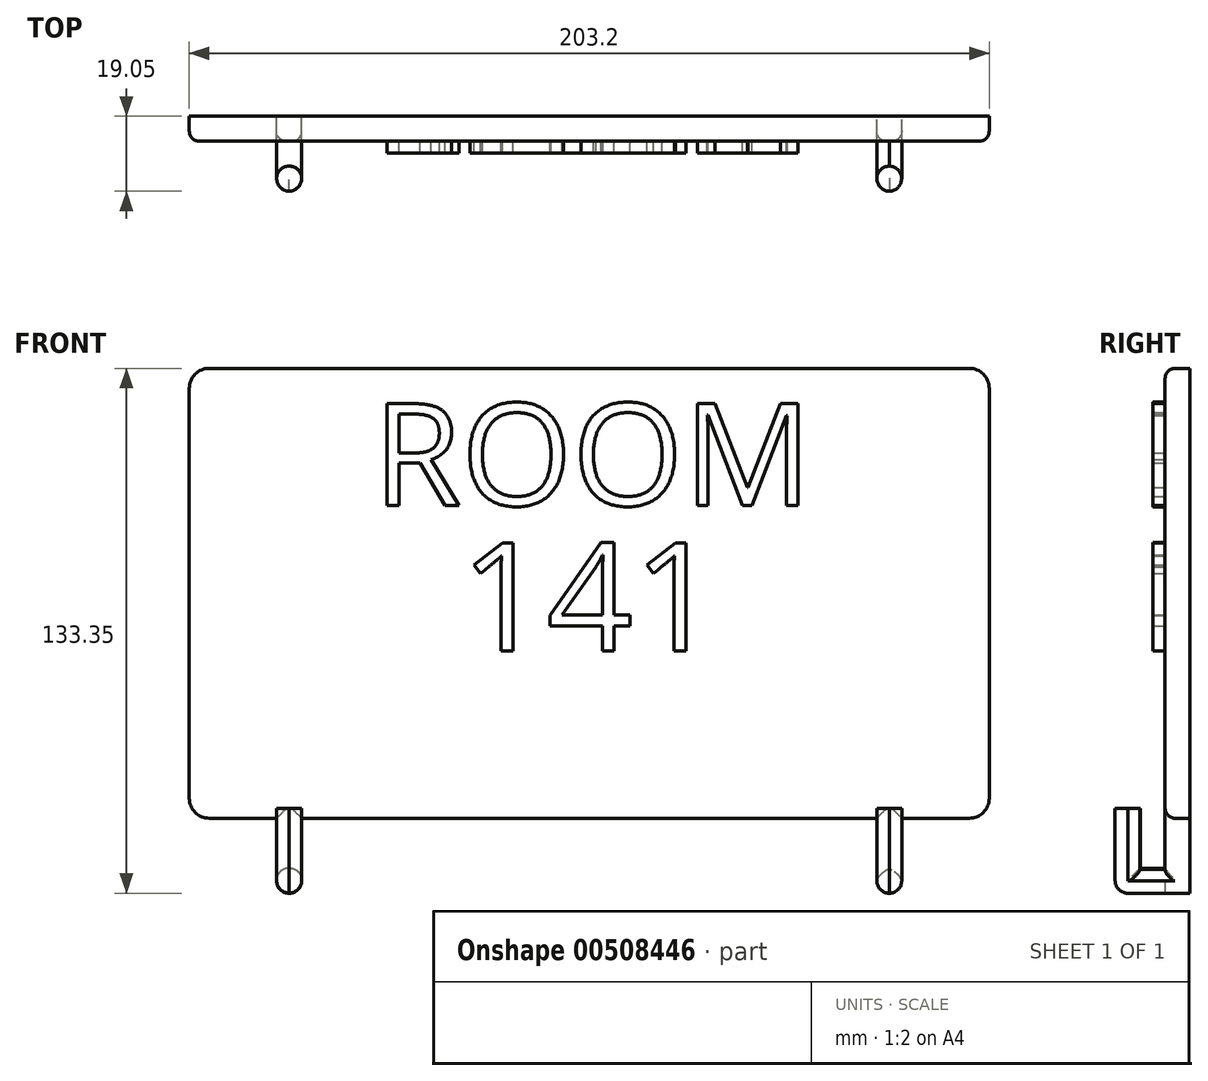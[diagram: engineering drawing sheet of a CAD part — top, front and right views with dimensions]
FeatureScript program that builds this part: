
annotation { "Feature Type Name" : "Feature", "Feature Type Description" : "" }
export const myFeature = defineFeature(function(context is Context, id is Id, definition is map)
    precondition{}
    {
        {
            var Q0;
            Q0=qCreatedBy(makeId("Front.planeOp"),FACE);
            var sketch = newSketch(context, id + "F0", { "sketchPlane" : qUnion([Q0])});
            skLineSegment(sketch, "E0.bottom", {"start": v(101.6, 57.15) * mm, "end": v(-101.6, 57.15) * mm});
            skLineSegment(sketch, "E0.top", {"start": v(101.6, -57.15) * mm, "end": v(-101.6, -57.15) * mm});
            skLineSegment(sketch, "E0.left", {"start": v(101.6, 57.15) * mm, "end": v(101.6, -57.15) * mm});
            skLineSegment(sketch, "E0.right", {"start": v(-101.6, 57.15) * mm, "end": v(-101.6, -57.15) * mm});
            skPoint(sketch, "E0.middle", {"position": v(0, 0) * mm});
            skSolve(sketch);
        }
        {
            var Q0;
            Q0=makeQuery(id+"F0.imprint","IMPRINT",FACE,{"disambiguationData":[TD([[makeQuery(id+"F0.imprint","IMPRINT",EDGE,{"derivedFrom":sQuery(id+"F0.wireOp",EDGE,"E0.bottom")}),1.0]])]});
            extrude(context, id + "F1", {"entities" : qUnion([Q0]), "depth" : 6.35 * mm});
        }
        {
            var Q0;
            Q0=makeQuery(id+"F1.opExtrude","SWEPT_FACE",FACE,{"disambiguationData":[OSD([sQuery(id+"F0.wireOp",EDGE,"E0.top")])]});
            var sketch = newSketch(context, id + "F2", { "sketchPlane" : qUnion([Q0])});
            skLineSegment(sketch, "E1.bottom", {"start": v(-73.07, 6.35) * mm, "end": v(-79.42, 6.35) * mm});
            skLineSegment(sketch, "E1.top", {"start": v(-73.07, 0) * mm, "end": v(-79.42, 0) * mm});
            skLineSegment(sketch, "E1.left", {"start": v(-73.07, 6.35) * mm, "end": v(-73.07, 0) * mm});
            skLineSegment(sketch, "E1.right", {"start": v(-79.42, 6.35) * mm, "end": v(-79.42, 0) * mm});
            skPoint(sketch, "E1.middle", {"position": v(-76.24, 3.17) * mm});
            skLineSegment(sketch, "E2.bottom", {"start": v(79.39, 6.35) * mm, "end": v(73.04, 6.35) * mm});
            skLineSegment(sketch, "E2.top", {"start": v(79.39, 0) * mm, "end": v(73.04, 0) * mm});
            skLineSegment(sketch, "E2.left", {"start": v(79.39, 6.35) * mm, "end": v(79.39, 0) * mm});
            skLineSegment(sketch, "E2.right", {"start": v(73.04, 6.35) * mm, "end": v(73.04, 0) * mm});
            skPoint(sketch, "E2.middle", {"position": v(76.21, 3.18) * mm});
            skSolve(sketch);
        }
        {
            var Q0;
            Q0 = qSketchRegion(id + "F2", true);
            extrude(context, id + "F3", {"entities" : qUnion([Q0]), "operationType" : NewBodyOperationType.ADD, "depth" : 19.05 * mm});
        }
        {
            var Q0;
            Q0=makeQuery(id+"F3.boolean.opBoolean","MERGE",FACE,{"derivedFrom":[makeQuery(id+"F1.opExtrude","CAP_FACE",FACE,{"disambiguationData":[OSD([sQuery(id+"F0.wireOp",EDGE,"E0.bottom"),sQuery(id+"F0.wireOp",EDGE,"E0.top"),sQuery(id+"F0.wireOp",EDGE,"E0.left"),sQuery(id+"F0.wireOp",EDGE,"E0.right")])],"isStart":false}),makeQuery(id+"F3.opExtrude","SWEPT_FACE",FACE,{"disambiguationData":[OSD([sQuery(id+"F2.wireOp",EDGE,"E1.bottom")])]}),makeQuery(id+"F3.opExtrude","SWEPT_FACE",FACE,{"disambiguationData":[OSD([sQuery(id+"F2.wireOp",EDGE,"E2.bottom")])]})]});
            var sketch = newSketch(context, id + "F4", { "sketchPlane" : qUnion([Q0])});
            skLineSegment(sketch, "E3.bottom", {"start": v(-79.42, -76.18) * mm, "end": v(-73.07, -76.18) * mm});
            skLineSegment(sketch, "E3.top", {"start": v(-79.42, -69.83) * mm, "end": v(-73.07, -69.83) * mm});
            skLineSegment(sketch, "E3.left", {"start": v(-79.42, -76.18) * mm, "end": v(-79.42, -69.83) * mm});
            skLineSegment(sketch, "E3.right", {"start": v(-73.07, -76.18) * mm, "end": v(-73.07, -69.83) * mm});
            skPoint(sketch, "E3.middle", {"position": v(-76.24, -73) * mm});
            skPoint(sketch, "E3.middle.positionSnap0", {"position": v(-76.24, -76.2) * mm});
            skPoint(sketch, "E3.centerSnap0", {"position": v(-76.24, -76.2) * mm});
            skPoint(sketch, "E4.cornerSnap0", {"position": v(79.39, -66.68) * mm});
            skPoint(sketch, "E5", {"position": v(76.21, -76.2) * mm});
            skLineSegment(sketch, "E6.bottom", {"start": v(73.04, -76.2) * mm, "end": v(79.39, -76.2) * mm});
            skLineSegment(sketch, "E6.top", {"start": v(73.04, -69.85) * mm, "end": v(79.39, -69.85) * mm});
            skLineSegment(sketch, "E6.left", {"start": v(73.04, -76.2) * mm, "end": v(73.04, -69.85) * mm});
            skLineSegment(sketch, "E6.right", {"start": v(79.39, -76.2) * mm, "end": v(79.39, -69.85) * mm});
            skSolve(sketch);
        }
        {
            var Q0;
            Q0 = qSketchRegion(id + "F4", true);
            extrude(context, id + "F5", {"entities" : qUnion([Q0]), "operationType" : NewBodyOperationType.ADD, "depth" : 12.7 * mm});
        }
        {
            var Q0;
            Q0=makeQuery(id+"F5.opExtrude","SWEPT_FACE",FACE,{"disambiguationData":[OSD([sQuery(id+"F4.wireOp",EDGE,"E6.top")])]});
            var sketch = newSketch(context, id + "F6", { "sketchPlane" : qUnion([Q0])});
            skLineSegment(sketch, "E7.bottom", {"start": v(73.04, -19.05) * mm, "end": v(79.39, -19.05) * mm});
            skLineSegment(sketch, "E7.top", {"start": v(73.04, -12.7) * mm, "end": v(79.39, -12.7) * mm});
            skLineSegment(sketch, "E7.left", {"start": v(73.04, -19.05) * mm, "end": v(73.04, -12.7) * mm});
            skLineSegment(sketch, "E7.right", {"start": v(79.39, -19.05) * mm, "end": v(79.39, -12.7) * mm});
            skLineSegment(sketch, "E8.bottom", {"start": v(-79.42, -19.04) * mm, "end": v(-73.07, -19.04) * mm});
            skLineSegment(sketch, "E8.top", {"start": v(-79.42, -12.7) * mm, "end": v(-73.07, -12.7) * mm});
            skLineSegment(sketch, "E8.left", {"start": v(-79.42, -19.04) * mm, "end": v(-79.42, -12.7) * mm});
            skLineSegment(sketch, "E8.right", {"start": v(-73.07, -19.04) * mm, "end": v(-73.07, -12.7) * mm});
            skSolve(sketch);
        }
        {
            var Q0;
            Q0 = qSketchRegion(id + "F6", true);
            extrude(context, id + "F7", {"entities" : qUnion([Q0]), "operationType" : NewBodyOperationType.ADD, "depth" : 15.24 * mm, "offsetDistance" : 25.4 * mm});
        }
        {
            var Q0;
            Q0=makeQuery(id+"F7.opExtrude","SWEPT_EDGE",EDGE,{"disambiguationData":[OSD([sQuery(id+"F6.wireOp",EDGE,"E8.bottom"),sQuery(id+"F6.wireOp",EDGE,"E8.left")])]});
            var Q1;
            Q1=makeQuery(id+"F7.opExtrude","SWEPT_EDGE",EDGE,{"disambiguationData":[OSD([sQuery(id+"F6.wireOp",EDGE,"E8.bottom"),sQuery(id+"F6.wireOp",EDGE,"E8.right")])]});
            fillet(context, id + "F8", {"entities" : qUnion([Q0, Q1]), "radius" : 3.3 * mm, "tangentPropagation" : true, "allowEdgeOverflow" : false});
        }
        {
            var Q0;
            Q0=makeQuery(id+"F5.opExtrude","SWEPT_EDGE",EDGE,{"disambiguationData":[OSD([sQuery(id+"F0.wireOp",EDGE,"E0.top"),sQuery(id+"F2.wireOp",EDGE,"E1.bottom"),sQuery(id+"F2.wireOp",EDGE,"E1.left"),sQuery(id+"F4.wireOp",EDGE,"E3.bottom"),sQuery(id+"F4.wireOp",EDGE,"E3.right")])]});
            var Q1;
            Q1=makeQuery(id+"F5.opExtrude","SWEPT_EDGE",EDGE,{"disambiguationData":[OSD([sQuery(id+"F0.wireOp",EDGE,"E0.top"),sQuery(id+"F2.wireOp",EDGE,"E1.bottom"),sQuery(id+"F2.wireOp",EDGE,"E1.right"),sQuery(id+"F4.wireOp",EDGE,"E3.bottom"),sQuery(id+"F4.wireOp",EDGE,"E3.left")])]});
            fillet(context, id + "F9", {"entities" : qUnion([Q0, Q1]), "radius" : 3.17 * mm, "tangentPropagation" : true, "allowEdgeOverflow" : false});
        }
        {
            var Q0;
            Q0=makeQuery(id+"F3.opExtrude","CAP_EDGE",EDGE,{"disambiguationData":[OSD([sQuery(id+"F2.wireOp",EDGE,"E1.left")])],"isStart":false});
            var Q1;
            Q1=makeQuery(id+"F3.opExtrude","CAP_EDGE",EDGE,{"disambiguationData":[OSD([sQuery(id+"F2.wireOp",EDGE,"E1.right")])],"isStart":false});
            fillet(context, id + "F10", {"entities" : qUnion([Q0, Q1]), "radius" : 3.17 * mm, "tangentPropagation" : true, "allowEdgeOverflow" : false});
        }
        {
            var Q0;
            Q0=makeQuery(id+"F7.opExtrude","SWEPT_EDGE",EDGE,{"disambiguationData":[OSD([sQuery(id+"F6.wireOp",EDGE,"E8.top"),sQuery(id+"F6.wireOp",EDGE,"E8.left")])]});
            var Q1;
            Q1=makeQuery(id+"F7.opExtrude","SWEPT_EDGE",EDGE,{"disambiguationData":[OSD([sQuery(id+"F6.wireOp",EDGE,"E8.top"),sQuery(id+"F6.wireOp",EDGE,"E8.right")])]});
            var Q2;
            {var subQ0=sQuery(id+"F2.wireOp",EDGE,"E1.right");var subQ1=sQuery(id+"F4.wireOp",EDGE,"E3.top");var subQ2=sQuery(id+"F4.wireOp",EDGE,"E3.left");Q2=makeQuery(id+"F7.boolean.opBoolean","SPLIT",EDGE,{"disambiguationData":[topologyDisambiguationEdgeConnected([makeQuery(id+"F5.opExtrude","SWEPT_FACE",FACE,{"disambiguationData":[OSD([subQ1])]})])],"derivedFrom":makeQuery(id+"F5.opExtrude","SWEPT_EDGE",EDGE,{"disambiguationData":[OSD([sQuery(id+"F0.wireOp",EDGE,"E0.top"),sQuery(id+"F2.wireOp",EDGE,"E1.bottom"),subQ0,subQ1,subQ2])]})});}
            var Q3;
            {var subQ0=sQuery(id+"F2.wireOp",EDGE,"E1.left");var subQ1=sQuery(id+"F4.wireOp",EDGE,"E3.right");var subQ2=sQuery(id+"F4.wireOp",EDGE,"E3.top");Q3=makeQuery(id+"F7.boolean.opBoolean","SPLIT",EDGE,{"disambiguationData":[topologyDisambiguationEdgeConnected([makeQuery(id+"F5.opExtrude","SWEPT_FACE",FACE,{"disambiguationData":[OSD([subQ2])]})])],"derivedFrom":makeQuery(id+"F5.opExtrude","SWEPT_EDGE",EDGE,{"disambiguationData":[OSD([sQuery(id+"F0.wireOp",EDGE,"E0.top"),sQuery(id+"F2.wireOp",EDGE,"E1.bottom"),subQ0,subQ2,subQ1])]})});}
            fillet(context, id + "F11", {"entities" : qUnion([Q0, Q1, Q2, Q3]), "radius" : 3.05 * mm, "tangentPropagation" : true, "allowEdgeOverflow" : false});
        }
        {
            var Q0;
            Q0=makeQuery(id+"F7.boolean.opBoolean","MERGE",EDGE,{"derivedFrom":[makeQuery(id+"F5.opExtrude","CAP_EDGE",EDGE,{"disambiguationData":[OSD([sQuery(id+"F4.wireOp",EDGE,"E6.left")])],"isStart":false}),makeQuery(id+"F7.opExtrude","SWEPT_EDGE",EDGE,{"disambiguationData":[OSD([sQuery(id+"F6.wireOp",EDGE,"E7.bottom"),sQuery(id+"F6.wireOp",EDGE,"E7.left")])]})]});
            var Q1;
            Q1=makeQuery(id+"F7.boolean.opBoolean","MERGE",EDGE,{"derivedFrom":[makeQuery(id+"F5.opExtrude","CAP_EDGE",EDGE,{"disambiguationData":[OSD([sQuery(id+"F4.wireOp",EDGE,"E6.right")])],"isStart":false}),makeQuery(id+"F7.opExtrude","SWEPT_EDGE",EDGE,{"disambiguationData":[OSD([sQuery(id+"F6.wireOp",EDGE,"E7.bottom"),sQuery(id+"F6.wireOp",EDGE,"E7.right")])]})]});
            fillet(context, id + "F12", {"entities" : qUnion([Q0, Q1]), "radius" : 3.3 * mm, "tangentPropagation" : true, "allowEdgeOverflow" : false});
        }
        {
            var Q0;
            Q0=makeQuery(id+"F7.opExtrude","SWEPT_EDGE",EDGE,{"disambiguationData":[OSD([sQuery(id+"F0.wireOp",EDGE,"E0.top"),sQuery(id+"F2.wireOp",EDGE,"E2.bottom"),sQuery(id+"F2.wireOp",EDGE,"E2.left"),sQuery(id+"F4.wireOp",EDGE,"E6.top"),sQuery(id+"F4.wireOp",EDGE,"E6.right"),sQuery(id+"F6.wireOp",EDGE,"E7.top"),sQuery(id+"F6.wireOp",EDGE,"E7.right")])]});
            var Q1;
            Q1=makeQuery(id+"F7.opExtrude","SWEPT_EDGE",EDGE,{"disambiguationData":[OSD([sQuery(id+"F0.wireOp",EDGE,"E0.top"),sQuery(id+"F2.wireOp",EDGE,"E2.bottom"),sQuery(id+"F2.wireOp",EDGE,"E2.right"),sQuery(id+"F4.wireOp",EDGE,"E6.top"),sQuery(id+"F4.wireOp",EDGE,"E6.left"),sQuery(id+"F6.wireOp",EDGE,"E7.top"),sQuery(id+"F6.wireOp",EDGE,"E7.left")])]});
            fillet(context, id + "F13", {"entities" : qUnion([Q0, Q1]), "radius" : 3.17 * mm, "tangentPropagation" : true, "allowEdgeOverflow" : false});
        }
        {
            var Q0;
            Q0=makeQuery(id+"F5.boolean.opBoolean","MERGE",EDGE,{"derivedFrom":[makeQuery(id+"F3.opExtrude","CAP_EDGE",EDGE,{"disambiguationData":[OSD([sQuery(id+"F2.wireOp",EDGE,"E2.right")])],"isStart":false}),makeQuery(id+"F5.opExtrude","SWEPT_EDGE",EDGE,{"disambiguationData":[OSD([sQuery(id+"F4.wireOp",EDGE,"E6.bottom"),sQuery(id+"F4.wireOp",EDGE,"E6.left")])]})]});
            var Q1;
            Q1=makeQuery(id+"F5.boolean.opBoolean","MERGE",EDGE,{"derivedFrom":[makeQuery(id+"F3.opExtrude","CAP_EDGE",EDGE,{"disambiguationData":[OSD([sQuery(id+"F2.wireOp",EDGE,"E2.left")])],"isStart":false}),makeQuery(id+"F5.opExtrude","SWEPT_EDGE",EDGE,{"disambiguationData":[OSD([sQuery(id+"F4.wireOp",EDGE,"E6.bottom"),sQuery(id+"F4.wireOp",EDGE,"E6.right")])]})]});
            fillet(context, id + "F14", {"entities" : qUnion([Q0, Q1]), "radius" : 3.17 * mm, "tangentPropagation" : true, "allowEdgeOverflow" : false});
        }
        {
            var Q0;
            Q0=makeQuery(id+"F5.opExtrude","SWEPT_EDGE",EDGE,{"disambiguationData":[OSD([sQuery(id+"F0.wireOp",EDGE,"E0.top"),sQuery(id+"F2.wireOp",EDGE,"E2.bottom"),sQuery(id+"F2.wireOp",EDGE,"E2.right"),sQuery(id+"F4.wireOp",EDGE,"E6.top"),sQuery(id+"F4.wireOp",EDGE,"E6.left")])]});
            var Q1;
            Q1=makeQuery(id+"F5.opExtrude","SWEPT_EDGE",EDGE,{"disambiguationData":[OSD([sQuery(id+"F0.wireOp",EDGE,"E0.top"),sQuery(id+"F2.wireOp",EDGE,"E2.bottom"),sQuery(id+"F2.wireOp",EDGE,"E2.left"),sQuery(id+"F4.wireOp",EDGE,"E6.top"),sQuery(id+"F4.wireOp",EDGE,"E6.right")])]});
            fillet(context, id + "F15", {"entities" : qUnion([Q0, Q1]), "radius" : 5.08 * mm, "tangentPropagation" : true, "allowEdgeOverflow" : false});
        }
        {
            var Q0;
            Q0=makeQuery(id+"F1.opExtrude","SWEPT_EDGE",EDGE,{"disambiguationData":[OSD([sQuery(id+"F0.wireOp",EDGE,"E0.top"),sQuery(id+"F0.wireOp",EDGE,"E0.left")])]});
            var Q1;
            Q1=makeQuery(id+"F1.opExtrude","SWEPT_EDGE",EDGE,{"disambiguationData":[OSD([sQuery(id+"F0.wireOp",EDGE,"E0.bottom"),sQuery(id+"F0.wireOp",EDGE,"E0.left")])]});
            var Q2;
            Q2=makeQuery(id+"F1.opExtrude","SWEPT_EDGE",EDGE,{"disambiguationData":[OSD([sQuery(id+"F0.wireOp",EDGE,"E0.bottom"),sQuery(id+"F0.wireOp",EDGE,"E0.right")])]});
            var Q3;
            Q3=makeQuery(id+"F1.opExtrude","SWEPT_EDGE",EDGE,{"disambiguationData":[OSD([sQuery(id+"F0.wireOp",EDGE,"E0.top"),sQuery(id+"F0.wireOp",EDGE,"E0.right")])]});
            fillet(context, id + "F16", {"entities" : qUnion([Q0, Q1, Q2, Q3]), "radius" : 5.08 * mm, "tangentPropagation" : true, "allowEdgeOverflow" : false});
        }
        {
            var Q0;
            Q0=makeQuery(id+"F1.opExtrude","CAP_EDGE",EDGE,{"disambiguationData":[OSD([sQuery(id+"F0.wireOp",EDGE,"E0.bottom")])],"isStart":false});
            var Q1;
            {var subQ0=sQuery(id+"F0.wireOp",EDGE,"E0.top");Q1=makeQuery(id+"F3.boolean.opBoolean","SPLIT",EDGE,{"disambiguationData":[TD([makeQuery(id+"F3.opExtrude","SWEPT_FACE",FACE,{"disambiguationData":[OSD([sQuery(id+"F2.wireOp",EDGE,"E1.left")])]})])],"derivedFrom":makeQuery(id+"F1.opExtrude","CAP_EDGE",EDGE,{"disambiguationData":[OSD([subQ0])],"isStart":false})});}
            var Q2;
            Q2=makeQuery(id+"F3.opExtrude","SWEPT_EDGE",EDGE,{"disambiguationData":[OSD([sQuery(id+"F0.wireOp",EDGE,"E0.top"),sQuery(id+"F2.wireOp",EDGE,"E2.bottom"),sQuery(id+"F2.wireOp",EDGE,"E2.right")])]});
            var Q3;
            Q3=makeQuery(id+"F3.opExtrude","SWEPT_EDGE",EDGE,{"disambiguationData":[OSD([sQuery(id+"F0.wireOp",EDGE,"E0.top"),sQuery(id+"F2.wireOp",EDGE,"E2.bottom"),sQuery(id+"F2.wireOp",EDGE,"E2.left")])]});
            var Q4;
            {var subQ0=sQuery(id+"F2.wireOp",EDGE,"E1.right");var subQ1=sQuery(id+"F2.wireOp",EDGE,"E1.bottom");var subQ2=sQuery(id+"F0.wireOp",EDGE,"E0.top");Q4=makeQuery(id+"F5.boolean.opBoolean","SPLIT",EDGE,{"disambiguationData":[TD([makeQuery(id+"F1.opExtrude","SWEPT_FACE",FACE,{"disambiguationData":[OSD([subQ2])]})])],"derivedFrom":makeQuery(id+"F3.opExtrude","SWEPT_EDGE",EDGE,{"disambiguationData":[OSD([subQ2,subQ1,subQ0])]})});}
            var Q5;
            {var subQ0=sQuery(id+"F2.wireOp",EDGE,"E1.bottom");var subQ1=sQuery(id+"F0.wireOp",EDGE,"E0.top");var subQ2=sQuery(id+"F2.wireOp",EDGE,"E1.left");Q5=makeQuery(id+"F5.boolean.opBoolean","SPLIT",EDGE,{"disambiguationData":[TD([makeQuery(id+"F1.opExtrude","SWEPT_FACE",FACE,{"disambiguationData":[OSD([subQ1])]})])],"derivedFrom":makeQuery(id+"F3.opExtrude","SWEPT_EDGE",EDGE,{"disambiguationData":[OSD([subQ1,subQ0,subQ2])]})});}
            fillet(context, id + "F17", {"entities" : qUnion([Q0, Q1, Q2, Q3, Q4, Q5]), "radius" : 2.54 * mm, "tangentPropagation" : true, "allowEdgeOverflow" : false});
        }
        {
            var Q0;
            {var subQ0=sQuery(id+"F0.wireOp",EDGE,"E0.bottom");var subQ1=sQuery(id+"F0.wireOp",EDGE,"E0.right");var subQ2=sQuery(id+"F0.wireOp",EDGE,"E0.top");var subQ3=sQuery(id+"F0.wireOp",EDGE,"E0.left");Q0=makeQuery(id+"F5.boolean.opBoolean","SPLIT",FACE,{"disambiguationData":[TD([makeQuery(id+"F1.opExtrude","SWEPT_FACE",FACE,{"disambiguationData":[OSD([subQ0])]})])],"derivedFrom":makeQuery(id+"F3.boolean.opBoolean","MERGE",FACE,{"derivedFrom":[makeQuery(id+"F1.opExtrude","CAP_FACE",FACE,{"disambiguationData":[OSD([subQ0,subQ2,subQ3,subQ1])],"isStart":false}),makeQuery(id+"F3.opExtrude","SWEPT_FACE",FACE,{"disambiguationData":[OSD([sQuery(id+"F2.wireOp",EDGE,"E1.bottom")])]}),makeQuery(id+"F3.opExtrude","SWEPT_FACE",FACE,{"disambiguationData":[OSD([sQuery(id+"F2.wireOp",EDGE,"E2.bottom")])]})]})});}
            var sketch = newSketch(context, id + "F18", { "sketchPlane" : qUnion([Q0])});
            skText(sketch, "E9", { "text": "ROOM", "fontName": "OpenSans-Regular.ttf"});
            const initialGuessF18  = {"E9": [-0.05492, 0.02232, 1, 0, 0.02608]};
            skSetInitialGuess(sketch, initialGuessF18);
            skSolve(sketch);
        }
        {
            var Q0;
            Q0 = qSketchRegion(id + "F18", true);
            extrude(context, id + "F19", {"entities" : qUnion([Q0]), "operationType" : NewBodyOperationType.ADD, "depth" : 3.05 * mm, "offsetDistance" : 25.4 * mm});
        }
        {
            var Q0;
            {var subQ1=sQuery(id+"F4.wireOp",EDGE,"E3.top");var subQ3=sQuery(id+"F2.wireOp",EDGE,"E1.bottom");var subQ4=sQuery(id+"F0.wireOp",EDGE,"E0.top");var subQ7=makeQuery(id+"F3.opExtrude","SWEPT_FACE",FACE,{"disambiguationData":[OSD([subQ3])]});var subQ12=sQuery(id+"F0.wireOp",EDGE,"E0.right");var subQ13=sQuery(id+"F0.wireOp",EDGE,"E0.left");var subQ14=sQuery(id+"F0.wireOp",EDGE,"E0.bottom");var subQ15=makeQuery(id+"F1.opExtrude","CAP_FACE",FACE,{"disambiguationData":[OSD([subQ14,subQ4,subQ13,subQ12])],"isStart":false});var subQ16=sQuery(id+"F2.wireOp",EDGE,"E2.bottom");var subQ17=makeQuery(id+"F3.opExtrude","SWEPT_FACE",FACE,{"disambiguationData":[OSD([subQ16])]});var subQ22=makeQuery(id+"F5.opExtrude","SWEPT_FACE",FACE,{"disambiguationData":[OSD([subQ1])]});var subQ28=makeQuery(id+"F5.boolean.opBoolean","SPLIT",FACE,{"disambiguationData":[TD([makeQuery(id+"F1.opExtrude","SWEPT_FACE",FACE,{"disambiguationData":[OSD([subQ14])]})])],"derivedFrom":makeQuery(id+"F3.boolean.opBoolean","MERGE",FACE,{"derivedFrom":[subQ15,subQ7,subQ17]})});Q0=makeQuery(id+"F19.boolean.opBoolean","SPLIT",FACE,{"disambiguationData":[TD([subQ22])],"derivedFrom":subQ28});}
            var sketch = newSketch(context, id + "F20", { "sketchPlane" : qUnion([Q0])});
            skText(sketch, "E10", { "text": "141", "fontName": "OpenSans-Regular.ttf"});
            const initialGuessF20  = {"E10": [-0.03279, -0.01462, 1, 0, 0.02766]};
            skSetInitialGuess(sketch, initialGuessF20);
            skSolve(sketch);
        }
        {
            var Q0;
            Q0 = qSketchRegion(id + "F20", true);
            extrude(context, id + "F21", {"entities" : qUnion([Q0]), "operationType" : NewBodyOperationType.ADD, "depth" : 3.05 * mm, "offsetDistance" : 25.4 * mm});
        }
        {
            var Q0;
            Q0=makeQuery(id+"F1.opExtrude","SWEPT_BODY",BODY,{"disambiguationData":[OSD([sQuery(id+"F0.wireOp",EDGE,"E0.bottom"),sQuery(id+"F0.wireOp",EDGE,"E0.top"),sQuery(id+"F0.wireOp",EDGE,"E0.left"),sQuery(id+"F0.wireOp",EDGE,"E0.right")])]});
            transform(context, id + "F22", {"entities" : qUnion([Q0]), "transformType" : TransformType.TRANSLATION_3D, "dx" : 0 * mm, "dy" : 0 * mm, "dz" : 0 * mm, "makeCopy" : true});
        }
        {
            var Q0;
            Q0=makeQuery(id+"F22.opPattern","COPY",BODY,{"derivedFrom":makeQuery(id+"F1.opExtrude","SWEPT_BODY",BODY,{"disambiguationData":[OSD([sQuery(id+"F0.wireOp",EDGE,"E0.bottom"),sQuery(id+"F0.wireOp",EDGE,"E0.top"),sQuery(id+"F0.wireOp",EDGE,"E0.left"),sQuery(id+"F0.wireOp",EDGE,"E0.right")])]}),"instanceName":"1"});
            deleteBodies(context, id + "F23", {"entities" : qUnion([Q0])});
        }
    });
